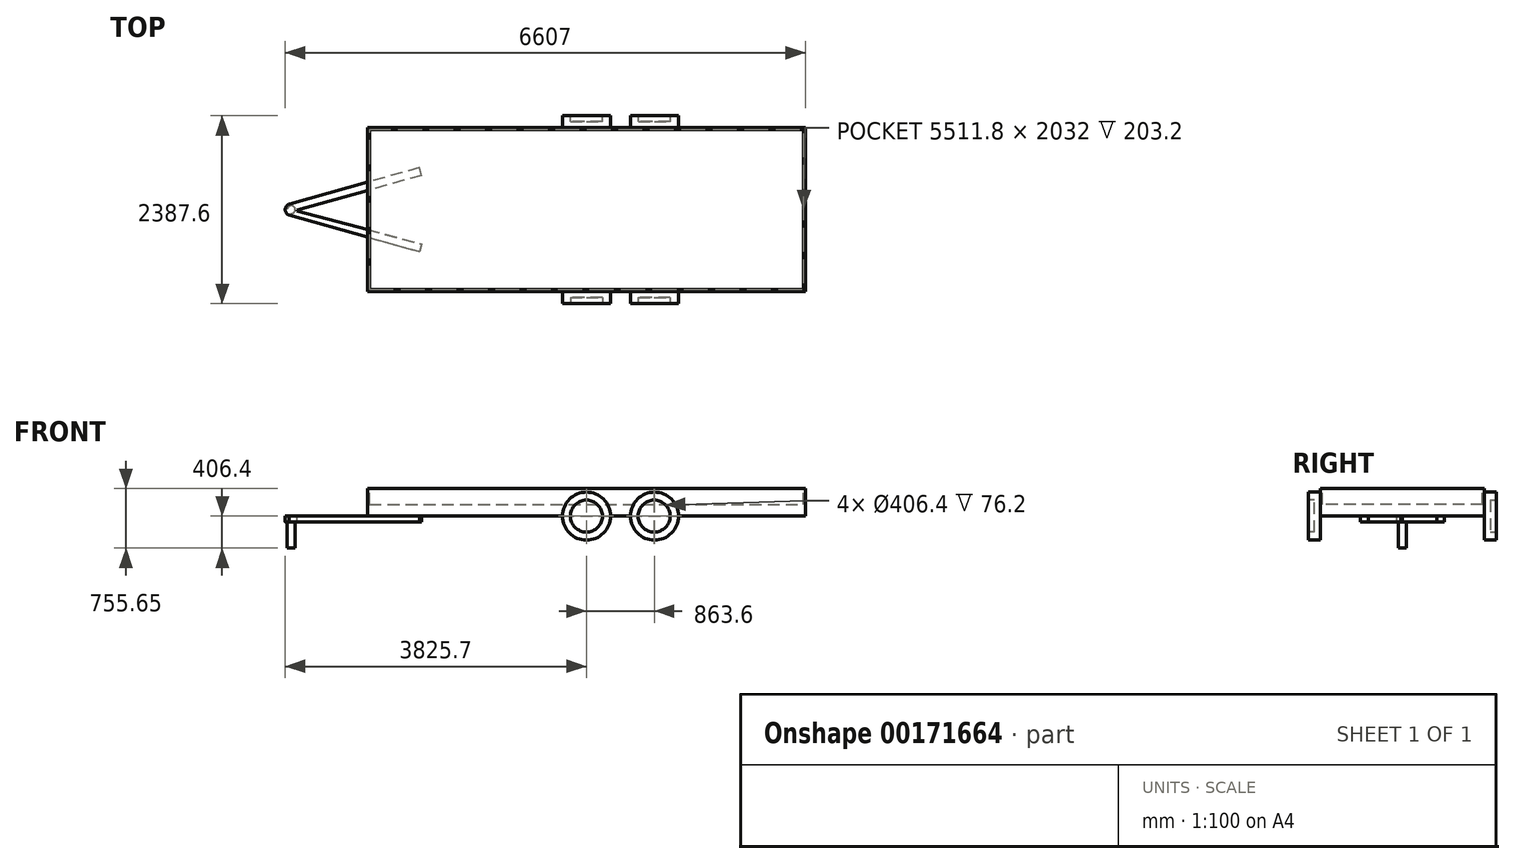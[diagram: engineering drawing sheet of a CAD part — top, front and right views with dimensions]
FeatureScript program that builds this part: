
annotation { "Feature Type Name" : "Feature", "Feature Type Description" : "" }
export const myFeature = defineFeature(function(context is Context, id is Id, definition is map)
    precondition{}
    {
        {
            var Q0;
            Q0=qCreatedBy(makeId("Top.planeOp"),FACE);
            var sketch = newSketch(context, id + "F0", { "sketchPlane" : qUnion([Q0])});
            skLineSegment(sketch, "E0.bottom", {"start": v(-2781.3, 1041.4) * mm, "end": v(2781.3, 1041.4) * mm});
            skLineSegment(sketch, "E0.top", {"start": v(-2781.3, -1041.4) * mm, "end": v(2781.3, -1041.4) * mm});
            skLineSegment(sketch, "E0.left", {"start": v(-2781.3, 1041.4) * mm, "end": v(-2781.3, -1041.4) * mm});
            skLineSegment(sketch, "E0.right", {"start": v(2781.3, 1041.4) * mm, "end": v(2781.3, -1041.4) * mm});
            skSolve(sketch);
        }
        {
            var Q0;
            Q0=makeQuery(id+"F0.imprint","IMPRINT",FACE,{"disambiguationData":[TD([[makeQuery(id+"F0.imprint","IMPRINT",EDGE,{"derivedFrom":sQuery(id+"F0.wireOp",EDGE,"E0.bottom")}),-1.0]])]});
            extrude(context, id + "F1", {"entities" : qUnion([Q0]), "depth" : 349.25 * mm});
        }
        {
            var Q0;
            Q0=makeQuery(id+"F1.opExtrude","CAP_FACE",FACE,{"disambiguationData":[OSD([sQuery(id+"F0.wireOp",EDGE,"E0.bottom"),sQuery(id+"F0.wireOp",EDGE,"E0.top"),sQuery(id+"F0.wireOp",EDGE,"E0.left"),sQuery(id+"F0.wireOp",EDGE,"E0.right")])],"isStart":false});
            var sketch = newSketch(context, id + "F2", { "sketchPlane" : qUnion([Q0])});
            skLineSegment(sketch, "E1.bottom", {"start": v(-2755.9, 1016) * mm, "end": v(2755.9, 1016) * mm});
            skLineSegment(sketch, "E1.top", {"start": v(-2755.9, -1016) * mm, "end": v(2755.9, -1016) * mm});
            skLineSegment(sketch, "E1.left", {"start": v(-2755.9, 1016) * mm, "end": v(-2755.9, -1016) * mm});
            skLineSegment(sketch, "E1.right", {"start": v(2755.9, 1016) * mm, "end": v(2755.9, -1016) * mm});
            skSolve(sketch);
        }
        {
            var Q0;
            Q0 = qSketchRegion(id + "F2", true);
            extrude(context, id + "F3", {"entities" : qUnion([Q0]), "operationType" : NewBodyOperationType.REMOVE, "oppositeDirection" : true, "depth" : 203.2 * mm});
        }
        {
            var Q0;
            Q0=makeQuery(id+"F1.opExtrude","SWEPT_FACE",FACE,{"disambiguationData":[OSD([sQuery(id+"F0.wireOp",EDGE,"E0.top")])]});
            var sketch = newSketch(context, id + "F4", { "sketchPlane" : qUnion([Q0])});
            skCircle(sketch, "E2", {"center": v(0, 0) * mm, "radius": 304.8 * mm});
            skCircle(sketch, "E3", {"center": v(863.6, 0) * mm, "radius": 304.8 * mm});
            skSolve(sketch);
        }
        {
            var Q0;
            {var subQ0=sQuery(id+"F4.wireOp",EDGE,"E2");var subQ1=makeQuery(id+"F1.opExtrude","CAP_EDGE",EDGE,{"disambiguationData":[OSD([sQuery(id+"F0.wireOp",EDGE,"E0.top")])],"isStart":true});var subQ2=makeQuery(id+"F4.imprint","INTERSECT",VERTEX,{"disambiguationData":[OD(0.0)],"derivedFrom":[subQ1,subQ0]});Q0=makeQuery(id+"F4.imprint","IMPRINT",FACE,{"disambiguationData":[TD([[makeQuery(id+"F4.imprint","IMPRINT",EDGE,{"disambiguationData":[TD([[subQ2,1.0]])],"derivedFrom":subQ0}),1.0]])]});}
            var Q1;
            {var subQ0=sQuery(id+"F4.wireOp",EDGE,"E2");var subQ1=makeQuery(id+"F1.opExtrude","CAP_EDGE",EDGE,{"disambiguationData":[OSD([sQuery(id+"F0.wireOp",EDGE,"E0.top")])],"isStart":true});var subQ2=makeQuery(id+"F4.imprint","INTERSECT",VERTEX,{"disambiguationData":[OD(0.0)],"derivedFrom":[subQ1,subQ0]});Q1=makeQuery(id+"F4.imprint","IMPRINT",FACE,{"disambiguationData":[TD([[makeQuery(id+"F4.imprint","IMPRINT",EDGE,{"disambiguationData":[TD([[subQ2,-1.0]])],"derivedFrom":subQ0}),1.0]])]});}
            var Q2;
            {var subQ0=sQuery(id+"F4.wireOp",EDGE,"E3");var subQ1=makeQuery(id+"F1.opExtrude","CAP_EDGE",EDGE,{"disambiguationData":[OSD([sQuery(id+"F0.wireOp",EDGE,"E0.top")])],"isStart":true});var subQ2=makeQuery(id+"F4.imprint","INTERSECT",VERTEX,{"disambiguationData":[OD(0.0)],"derivedFrom":[subQ1,subQ0]});Q2=makeQuery(id+"F4.imprint","IMPRINT",FACE,{"disambiguationData":[TD([[makeQuery(id+"F4.imprint","IMPRINT",EDGE,{"disambiguationData":[TD([[subQ2,1.0]])],"derivedFrom":subQ0}),1.0]])]});}
            var Q3;
            {var subQ0=sQuery(id+"F4.wireOp",EDGE,"E3");var subQ1=makeQuery(id+"F1.opExtrude","CAP_EDGE",EDGE,{"disambiguationData":[OSD([sQuery(id+"F0.wireOp",EDGE,"E0.top")])],"isStart":true});var subQ2=makeQuery(id+"F4.imprint","INTERSECT",VERTEX,{"disambiguationData":[OD(0.0)],"derivedFrom":[subQ1,subQ0]});Q3=makeQuery(id+"F4.imprint","IMPRINT",FACE,{"disambiguationData":[TD([[makeQuery(id+"F4.imprint","IMPRINT",EDGE,{"disambiguationData":[TD([[subQ2,-1.0]])],"derivedFrom":subQ0}),1.0]])]});}
            extrude(context, id + "F5", {"entities" : qUnion([Q0, Q1, Q2, Q3]), "operationType" : NewBodyOperationType.ADD, "depth" : 152.4 * mm});
        }
        {
            var Q0;
            Q0=makeQuery(id+"F5.opExtrude","CAP_FACE",FACE,{"disambiguationData":[OSD([sQuery(id+"F4.wireOp",EDGE,"E2")])],"isStart":false});
            var sketch = newSketch(context, id + "F6", { "sketchPlane" : qUnion([Q0])});
            skCircle(sketch, "E4", {"center": v(0, 0) * mm, "radius": 203.2 * mm});
            skCircle(sketch, "E5", {"center": v(860.16, 0) * mm, "radius": 203.2 * mm});
            skSolve(sketch);
        }
        {
            var Q0;
            Q0=makeQuery(id+"F6.imprint","IMPRINT",FACE,{"disambiguationData":[TD([[makeQuery(id+"F6.imprint","IMPRINT",EDGE,{"derivedFrom":sQuery(id+"F6.wireOp",EDGE,"E4")}),1.0]])]});
            var Q1;
            Q1=makeQuery(id+"F6.imprint","IMPRINT",FACE,{"disambiguationData":[TD([[makeQuery(id+"F6.imprint","IMPRINT",EDGE,{"derivedFrom":sQuery(id+"F6.wireOp",EDGE,"E5")}),1.0]])]});
            extrude(context, id + "F7", {"entities" : qUnion([Q0, Q1]), "operationType" : NewBodyOperationType.REMOVE, "oppositeDirection" : true, "depth" : 76.2 * mm});
        }
        {
            var Q0;
            Q0=makeQuery(id+"F1.opExtrude","SWEPT_FACE",FACE,{"disambiguationData":[OSD([sQuery(id+"F0.wireOp",EDGE,"E0.bottom")])]});
            var sketch = newSketch(context, id + "F8", { "sketchPlane" : qUnion([Q0])});
            skCircle(sketch, "E6", {"center": v(0, 0) * mm, "radius": 304.8 * mm});
            skCircle(sketch, "E7", {"center": v(-863.6, 0) * mm, "radius": 304.8 * mm});
            skSolve(sketch);
        }
        {
            var Q0;
            {var subQ0=sQuery(id+"F8.wireOp",EDGE,"E7");var subQ1=makeQuery(id+"F1.opExtrude","CAP_EDGE",EDGE,{"disambiguationData":[OSD([sQuery(id+"F0.wireOp",EDGE,"E0.bottom")])],"isStart":true});var subQ2=makeQuery(id+"F8.imprint","INTERSECT",VERTEX,{"disambiguationData":[OD(0.0)],"derivedFrom":[subQ1,subQ0]});Q0=makeQuery(id+"F8.imprint","IMPRINT",FACE,{"disambiguationData":[TD([[makeQuery(id+"F8.imprint","IMPRINT",EDGE,{"disambiguationData":[TD([[subQ2,1.0]])],"derivedFrom":subQ0}),1.0]])]});}
            var Q1;
            {var subQ0=sQuery(id+"F8.wireOp",EDGE,"E7");var subQ1=makeQuery(id+"F1.opExtrude","CAP_EDGE",EDGE,{"disambiguationData":[OSD([sQuery(id+"F0.wireOp",EDGE,"E0.bottom")])],"isStart":true});var subQ2=makeQuery(id+"F8.imprint","INTERSECT",VERTEX,{"disambiguationData":[OD(0.0)],"derivedFrom":[subQ1,subQ0]});Q1=makeQuery(id+"F8.imprint","IMPRINT",FACE,{"disambiguationData":[TD([[makeQuery(id+"F8.imprint","IMPRINT",EDGE,{"disambiguationData":[TD([[subQ2,-1.0]])],"derivedFrom":subQ0}),1.0]])]});}
            var Q2;
            {var subQ0=sQuery(id+"F8.wireOp",EDGE,"E6");var subQ1=makeQuery(id+"F1.opExtrude","CAP_EDGE",EDGE,{"disambiguationData":[OSD([sQuery(id+"F0.wireOp",EDGE,"E0.bottom")])],"isStart":true});var subQ2=makeQuery(id+"F8.imprint","INTERSECT",VERTEX,{"disambiguationData":[OD(0.0)],"derivedFrom":[subQ1,subQ0]});Q2=makeQuery(id+"F8.imprint","IMPRINT",FACE,{"disambiguationData":[TD([[makeQuery(id+"F8.imprint","IMPRINT",EDGE,{"disambiguationData":[TD([[subQ2,1.0]])],"derivedFrom":subQ0}),1.0]])]});}
            var Q3;
            {var subQ0=sQuery(id+"F8.wireOp",EDGE,"E6");var subQ1=makeQuery(id+"F1.opExtrude","CAP_EDGE",EDGE,{"disambiguationData":[OSD([sQuery(id+"F0.wireOp",EDGE,"E0.bottom")])],"isStart":true});var subQ2=makeQuery(id+"F8.imprint","INTERSECT",VERTEX,{"disambiguationData":[OD(0.0)],"derivedFrom":[subQ1,subQ0]});Q3=makeQuery(id+"F8.imprint","IMPRINT",FACE,{"disambiguationData":[TD([[makeQuery(id+"F8.imprint","IMPRINT",EDGE,{"disambiguationData":[TD([[subQ2,-1.0]])],"derivedFrom":subQ0}),1.0]])]});}
            extrude(context, id + "F9", {"entities" : qUnion([Q0, Q1, Q2, Q3]), "operationType" : NewBodyOperationType.ADD, "depth" : 152.4 * mm});
        }
        {
            var Q0;
            Q0=makeQuery(id+"F9.opExtrude","CAP_FACE",FACE,{"disambiguationData":[OSD([sQuery(id+"F8.wireOp",EDGE,"E7")])],"isStart":false});
            var sketch = newSketch(context, id + "F10", { "sketchPlane" : qUnion([Q0])});
            skCircle(sketch, "E8", {"center": v(0, 0) * mm, "radius": 203.2 * mm});
            skCircle(sketch, "E9", {"center": v(-863.6, 0) * mm, "radius": 203.2 * mm});
            skSolve(sketch);
        }
        {
            var Q0;
            Q0=makeQuery(id+"F10.imprint","IMPRINT",FACE,{"disambiguationData":[TD([[makeQuery(id+"F10.imprint","IMPRINT",EDGE,{"derivedFrom":sQuery(id+"F10.wireOp",EDGE,"E9")}),1.0]])]});
            var Q1;
            Q1=makeQuery(id+"F10.imprint","IMPRINT",FACE,{"disambiguationData":[TD([[makeQuery(id+"F10.imprint","IMPRINT",EDGE,{"derivedFrom":sQuery(id+"F10.wireOp",EDGE,"E8")}),1.0]])]});
            extrude(context, id + "F11", {"entities" : qUnion([Q0, Q1]), "operationType" : NewBodyOperationType.REMOVE, "oppositeDirection" : true, "depth" : 76.2 * mm});
        }
        {
            var Q0;
            Q0=makeQuery(id+"F1.opExtrude","CAP_FACE",FACE,{"disambiguationData":[OSD([sQuery(id+"F0.wireOp",EDGE,"E0.bottom"),sQuery(id+"F0.wireOp",EDGE,"E0.top"),sQuery(id+"F0.wireOp",EDGE,"E0.left"),sQuery(id+"F0.wireOp",EDGE,"E0.right")])],"isStart":true});
            var sketch = newSketch(context, id + "F12", { "sketchPlane" : qUnion([Q0])});
            skArc(sketch, "E10", {"start": v(-3759.64, 75.52) * mm, "mid": v(-3825.52, 5.27) * mm, "end": v(-3769.97, -73.4) * mm});
            skLineSegment(sketch, "E11", {"start": v(-3675.8, 19.38) * mm, "end": v(-2095.06, 435.14) * mm});
            skLineSegment(sketch, "E12", {"start": v(-2095.06, 435.14) * mm, "end": v(-2120.9, 533.4) * mm});
            skLineSegment(sketch, "E13", {"start": v(-2120.9, -533.4) * mm, "end": v(-3769.97, -73.4) * mm});
            skLineSegment(sketch, "E14", {"start": v(-2095.06, -435.14) * mm, "end": v(-2120.9, -533.4) * mm});
            skLineSegment(sketch, "E15", {"start": v(-2095.06, -435.14) * mm, "end": v(-3673.47, 5.15) * mm});
            skLineSegment(sketch, "E16", {"start": v(-3779.97, 69.84) * mm, "end": v(-2120.9, 533.4) * mm});
            skArc(sketch, "E17.trimOffspring", {"start": v(-3673.47, 5.15) * mm, "mid": v(-3674.3, 12.32) * mm, "end": v(-3675.8, 19.38) * mm});
            skSolve(sketch);
        }
        {
            var Q0;
            {var subQ0=sQuery(id+"F12.wireOp",EDGE,"E17.trimOffspring");Q0=makeQuery(id+"F12.imprint","IMPRINT",FACE,{"disambiguationData":[TD([[makeQuery(id+"F12.imprint","IMPRINT",EDGE,{"derivedFrom":subQ0}),1.0]])]});}
            var Q1;
            {var subQ0=sQuery(id+"F12.wireOp",EDGE,"E12");Q1=makeQuery(id+"F12.imprint","IMPRINT",FACE,{"disambiguationData":[TD([[makeQuery(id+"F12.imprint","IMPRINT",EDGE,{"derivedFrom":subQ0}),1.0]])]});}
            var Q2;
            {var subQ0=sQuery(id+"F12.wireOp",EDGE,"E14");Q2=makeQuery(id+"F12.imprint","IMPRINT",FACE,{"disambiguationData":[TD([[makeQuery(id+"F12.imprint","IMPRINT",EDGE,{"derivedFrom":subQ0}),-1.0]])]});}
            extrude(context, id + "F13", {"entities" : qUnion([Q0, Q1, Q2]), "depth" : 76.2 * mm});
        }
        {
            var Q0;
            Q0=makeQuery(id+"F13.opExtrude","CAP_FACE",FACE,{"disambiguationData":[OSD([sQuery(id+"F12.wireOp",EDGE,"E10"),sQuery(id+"F12.wireOp",EDGE,"E11"),sQuery(id+"F12.wireOp",EDGE,"E12"),sQuery(id+"F12.wireOp",EDGE,"E13"),sQuery(id+"F12.wireOp",EDGE,"E14"),sQuery(id+"F12.wireOp",EDGE,"E15"),sQuery(id+"F12.wireOp",EDGE,"E16"),sQuery(id+"F12.wireOp",EDGE,"E17.trimOffspring")])],"isStart":false});
            var sketch = newSketch(context, id + "F14", { "sketchPlane" : qUnion([Q0])});
            skCircle(sketch, "E18", {"center": v(-3749.5, 0) * mm, "radius": 50.8 * mm});
            skSolve(sketch);
        }
        {
            var Q0;
            Q0=makeQuery(id+"F14.imprint","IMPRINT",FACE,{"disambiguationData":[TD([[makeQuery(id+"F14.imprint","IMPRINT",EDGE,{"derivedFrom":sQuery(id+"F14.wireOp",EDGE,"E18")}),1.0]])]});
            extrude(context, id + "F15", {"entities" : qUnion([Q0]), "depth" : 330.2 * mm});
        }
    });
